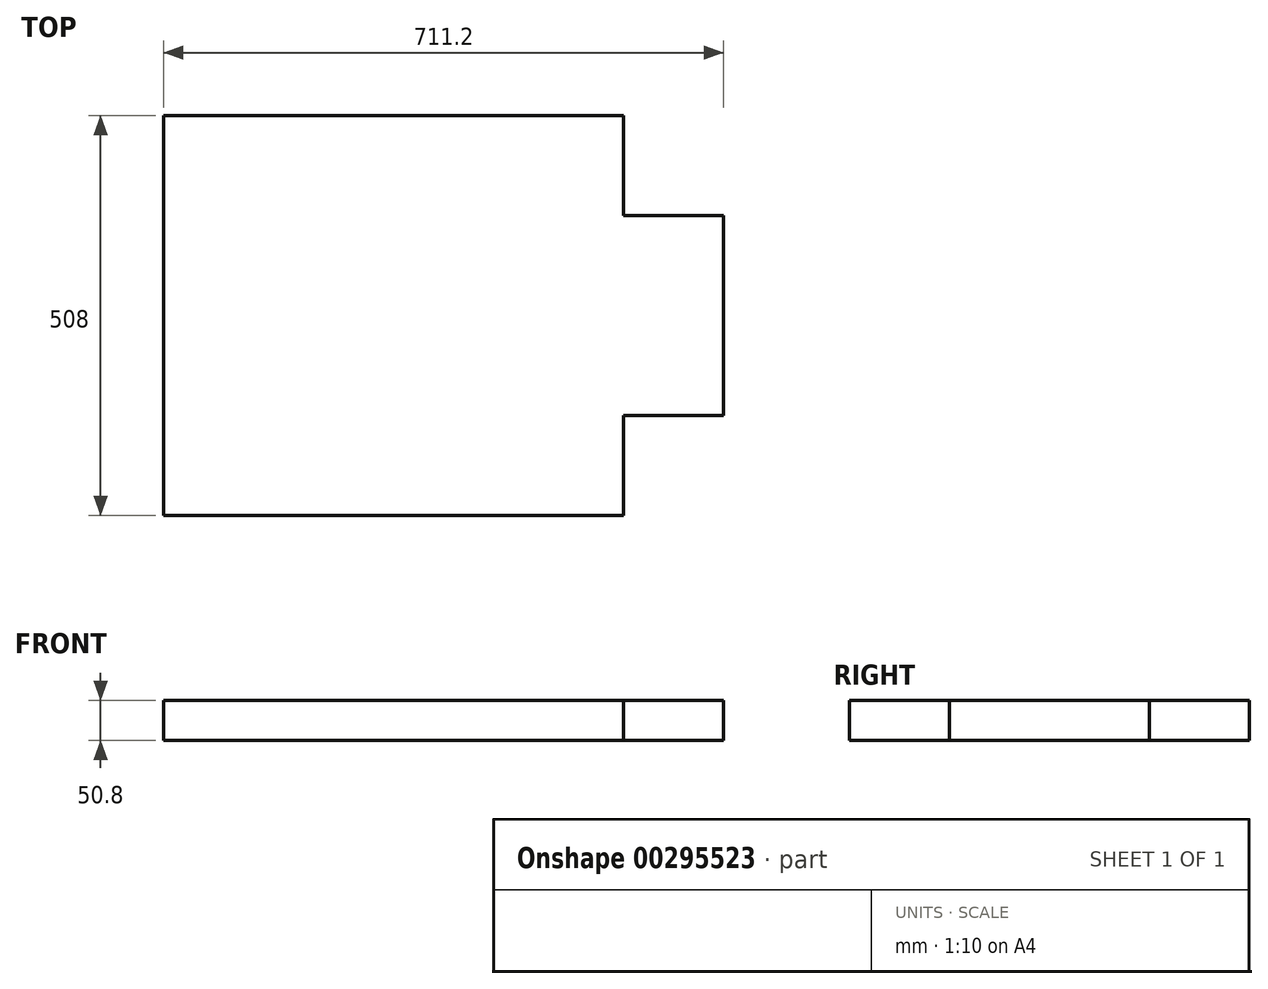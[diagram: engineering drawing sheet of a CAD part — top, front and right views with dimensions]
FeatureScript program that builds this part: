
annotation { "Feature Type Name" : "Feature", "Feature Type Description" : "" }
export const myFeature = defineFeature(function(context is Context, id is Id, definition is map)
    precondition{}
    {
        {
            var Q0;
            Q0=qCreatedBy(makeId("Top.planeOp"),FACE);
            var sketch = newSketch(context, id + "F0", { "sketchPlane" : qUnion([Q0])});
            skLineSegment(sketch, "E0.bottom", {"start": v(0, 0) * mm, "end": v(254, 0) * mm});
            skLineSegment(sketch, "E0.top", {"start": v(0, 508) * mm, "end": v(254, 508) * mm});
            skLineSegment(sketch, "E0.left", {"start": v(0, 0) * mm, "end": v(0, 0) * mm});
            skLineSegment(sketch, "E0.right", {"start": v(254, 0) * mm, "end": v(254, 508) * mm});
            skLineSegment(sketch, "E1.bottom", {"start": v(0, 0) * mm, "end": v(-330.2, 0) * mm});
            skLineSegment(sketch, "E1.top", {"start": v(0, 508) * mm, "end": v(-330.2, 508) * mm});
            skLineSegment(sketch, "E1.right", {"start": v(-330.2, 0) * mm, "end": v(-330.2, 508) * mm});
            skLineSegment(sketch, "E2.trimOffspring", {"start": v(0, 508) * mm, "end": v(0, 508) * mm});
            skSolve(sketch);
        }
        {
            var Q0;
            Q0=makeQuery(id+"F0.imprint","IMPRINT",FACE,{"disambiguationData":[TD([[makeQuery(id+"F0.imprint","IMPRINT",EDGE,{"derivedFrom":sQuery(id+"F0.wireOp",EDGE,"E0.bottom")}),1.0]])]});
            extrude(context, id + "F1", {"entities" : qUnion([Q0]), "depth" : 50.8 * mm});
        }
        {
            var Q0;
            Q0=makeQuery(id+"F1.opExtrude","SWEPT_FACE",FACE,{"disambiguationData":[OSD([sQuery(id+"F0.wireOp",EDGE,"E0.right")])]});
            var sketch = newSketch(context, id + "F2", { "sketchPlane" : qUnion([Q0])});
            skLineSegment(sketch, "E3.bottom", {"start": v(127, 50.8) * mm, "end": v(381, 50.8) * mm});
            skLineSegment(sketch, "E3.top", {"start": v(127, 0) * mm, "end": v(381, 0) * mm});
            skLineSegment(sketch, "E3.left", {"start": v(127, 50.8) * mm, "end": v(127, 0) * mm});
            skLineSegment(sketch, "E3.right", {"start": v(381, 50.8) * mm, "end": v(381, 0) * mm});
            skSolve(sketch);
        }
        {
            var Q0;
            Q0=makeQuery(id+"F2.imprint","IMPRINT",FACE,{"disambiguationData":[TD([[makeQuery(id+"F2.imprint","IMPRINT",EDGE,{"derivedFrom":sQuery(id+"F2.wireOp",EDGE,"E3.bottom")}),-1.0]])]});
            extrude(context, id + "F3", {"entities" : qUnion([Q0]), "operationType" : NewBodyOperationType.ADD, "depth" : 127 * mm});
        }
    });
